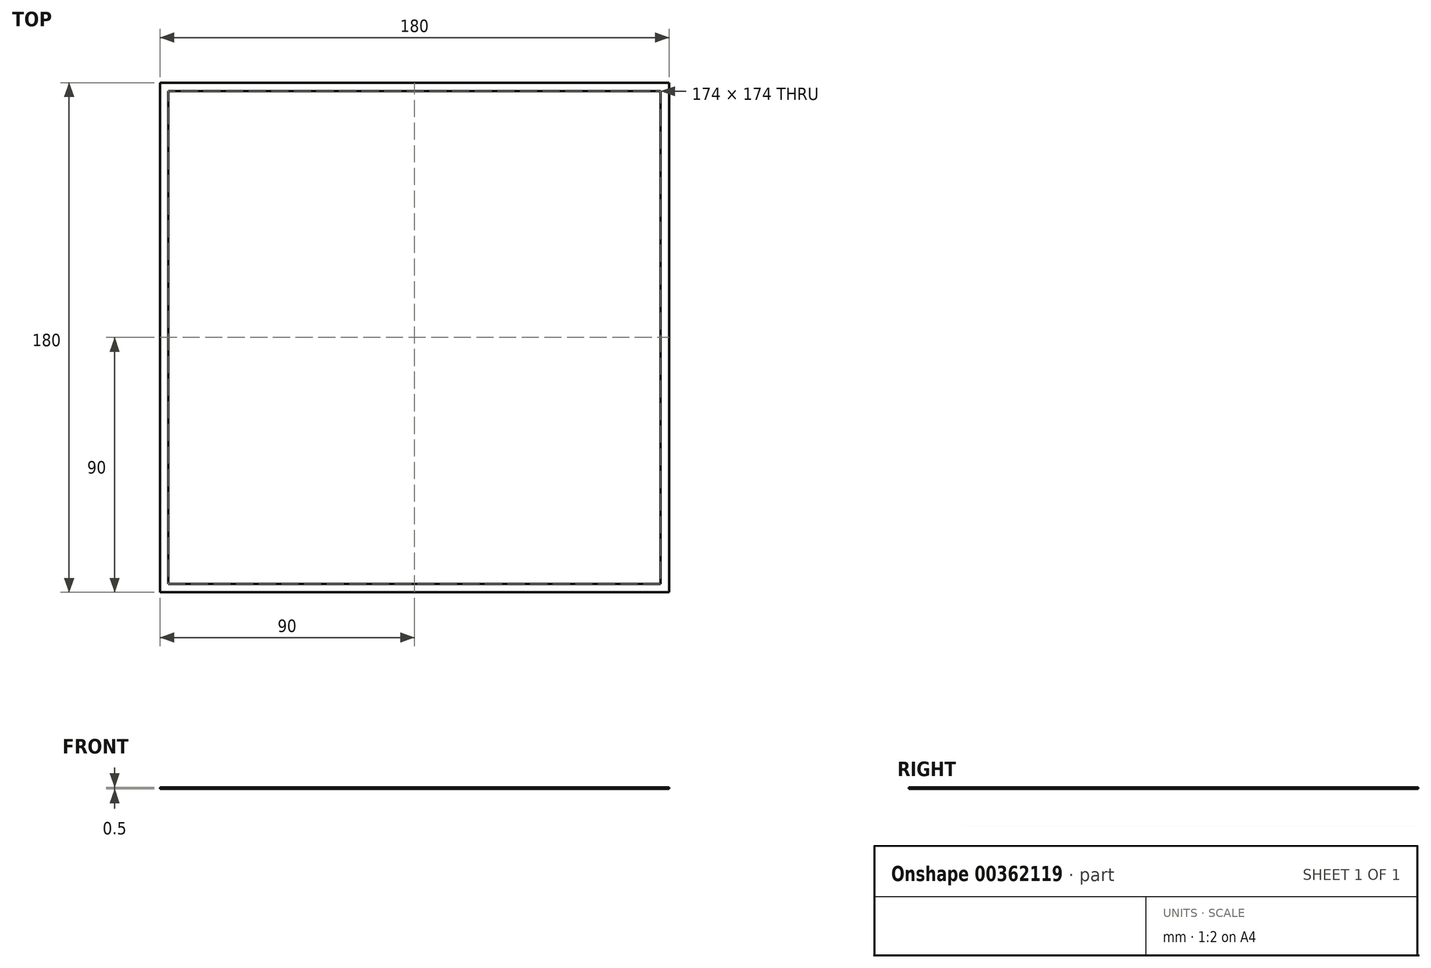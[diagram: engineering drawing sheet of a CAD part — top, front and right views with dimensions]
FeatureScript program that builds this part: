
annotation { "Feature Type Name" : "Feature", "Feature Type Description" : "" }
export const myFeature = defineFeature(function(context is Context, id is Id, definition is map)
    precondition{}
    {
        {
            var Q0;
            Q0=qCreatedBy(makeId("Top.planeOp"),FACE);
            var sketch = newSketch(context, id + "F0", { "sketchPlane" : qUnion([Q0])});
            skLineSegment(sketch, "E0.bottom", {"start": v(-90, 90) * mm, "end": v(90, 90) * mm});
            skLineSegment(sketch, "E0.top", {"start": v(-90, -90) * mm, "end": v(90, -90) * mm});
            skLineSegment(sketch, "E0.left", {"start": v(-90, 90) * mm, "end": v(-90, -90) * mm});
            skLineSegment(sketch, "E0.right", {"start": v(90, 90) * mm, "end": v(90, -90) * mm});
            skPoint(sketch, "E0.middle", {"position": v(0, 0) * mm});
            skLineSegment(sketch, "E1.bottom", {"start": v(-87, 87) * mm, "end": v(87, 87) * mm});
            skLineSegment(sketch, "E1.top", {"start": v(-87, -87) * mm, "end": v(87, -87) * mm});
            skLineSegment(sketch, "E1.left", {"start": v(-87, 87) * mm, "end": v(-87, -87) * mm});
            skLineSegment(sketch, "E1.right", {"start": v(87, 87) * mm, "end": v(87, -87) * mm});
            skSolve(sketch);
        }
        {
            var Q0;
            Q0=makeQuery(id+"F0.imprint","IMPRINT",FACE,{"disambiguationData":[TD([[makeQuery(id+"F0.imprint","IMPRINT",EDGE,{"derivedFrom":sQuery(id+"F0.wireOp",EDGE,"E0.bottom")}),-1.0]])]});
            extrude(context, id + "F1", {"entities" : qUnion([Q0]), "depth" : 0.5 * mm, "offsetDistance" : 25 * mm});
        }
    });
